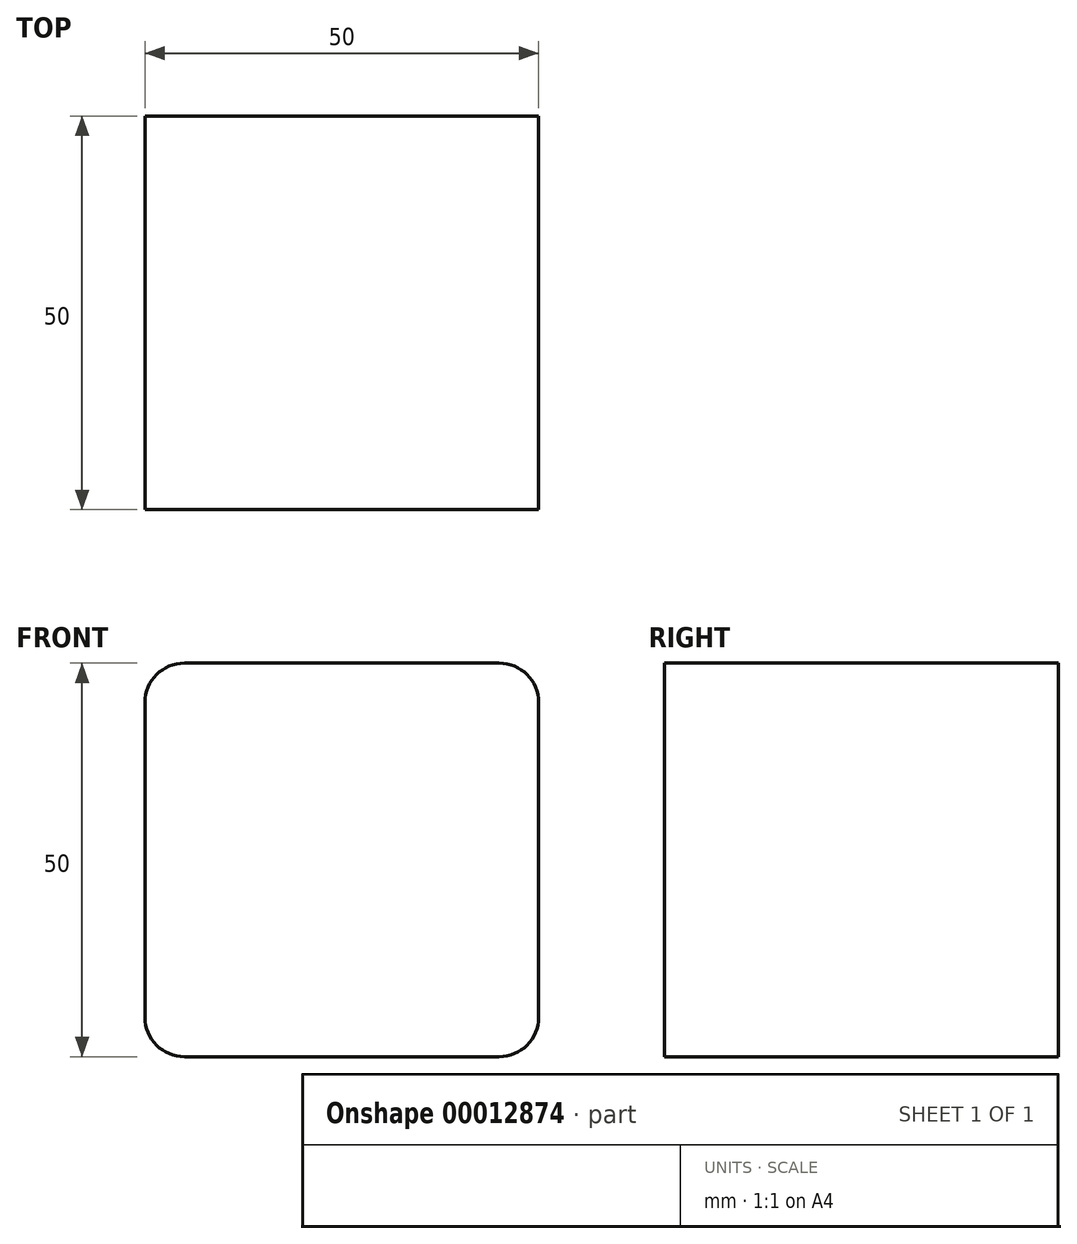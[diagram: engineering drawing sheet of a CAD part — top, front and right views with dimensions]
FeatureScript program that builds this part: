
annotation { "Feature Type Name" : "Feature", "Feature Type Description" : "" }
export const myFeature = defineFeature(function(context is Context, id is Id, definition is map)
    precondition{}
    {
        {
            var Q0;
            Q0=qCreatedBy(makeId("Front.planeOp"),FACE);
            var sketch = newSketch(context, id + "F0", { "sketchPlane" : qUnion([Q0])});
            skLineSegment(sketch, "E0.bottom", {"start": v(-33.7, 44.4) * mm, "end": v(16.3, 44.4) * mm});
            skLineSegment(sketch, "E0.top", {"start": v(-33.7, -5.6) * mm, "end": v(16.3, -5.6) * mm});
            skLineSegment(sketch, "E0.left", {"start": v(-33.7, 44.4) * mm, "end": v(-33.7, -5.6) * mm});
            skLineSegment(sketch, "E0.right", {"start": v(16.3, 44.4) * mm, "end": v(16.3, -5.6) * mm});
            skSolve(sketch);
        }
        {
            var Q0;
            Q0=makeQuery(id+"F0.imprint","IMPRINT",FACE,{"disambiguationData":[TD([[makeQuery(id+"F0.imprint","IMPRINT",EDGE,{"derivedFrom":sQuery(id+"F0.wireOp",EDGE,"E0.bottom")}),-1.0]])]});
            extrude(context, id + "F1", {"entities" : qUnion([Q0]), "depth" : 50 * mm});
        }
        {
            var Q0;
            Q0=makeQuery(id+"F1.opExtrude","SWEPT_EDGE",EDGE,{"disambiguationData":[OSD([sQuery(id+"F0.wireOp",EDGE,"E0.bottom"),sQuery(id+"F0.wireOp",EDGE,"E0.left")])]});
            var Q1;
            Q1=makeQuery(id+"F1.opExtrude","SWEPT_EDGE",EDGE,{"disambiguationData":[OSD([sQuery(id+"F0.wireOp",EDGE,"E0.bottom"),sQuery(id+"F0.wireOp",EDGE,"E0.right")])]});
            var Q2;
            Q2=makeQuery(id+"F1.opExtrude","SWEPT_EDGE",EDGE,{"disambiguationData":[OSD([sQuery(id+"F0.wireOp",EDGE,"E0.top"),sQuery(id+"F0.wireOp",EDGE,"E0.right")])]});
            var Q3;
            Q3=makeQuery(id+"F1.opExtrude","SWEPT_EDGE",EDGE,{"disambiguationData":[OSD([sQuery(id+"F0.wireOp",EDGE,"E0.top"),sQuery(id+"F0.wireOp",EDGE,"E0.left")])]});
            fillet(context, id + "F2", {"entities" : qUnion([Q0, Q1, Q2, Q3]), "radius" : 5 * mm, "tangentPropagation" : true, "allowEdgeOverflow" : false});
        }
    });
